# Revit family: Shower-Valve_Trim-KOHLER-Composed-K-T73140BR
name_source: partatom
category: Specialty Equipment
revit_build: Autodesk Revit 2017 (Build: 20160225_1515(x64)
units: mm (PartAtom-declared; Revit-internal decimal feet)

## family parameters
Cut with Voids When Loaded = No
Host = Face
OmniClass Number = 23.31.25.00
OmniClass Title = Toilet and Bath Specialties
Part Type = Normal
Room Calculation Point = No
Round Connector Dimension = Use Diameter
Shared = No

## types (3) — shared parameters
ADA Compliant = Yes
Assembly Code = C1030200
Date Modified = 05/26/2021
Default Elevation = 42"
Description = shower diverter valve
Height = 3 7/8"
Length = 3 5/16"
Manufacturer = KOHLER Co.
Master Format 2014 = 10 28 00
Master Format 2014 Name = Toilet, Bath, and Laundry Accessories
Material = Premium Metal Construction
Product Name = COMPOSED
Product Page URL = https://br.kohler.com
URL = https://br.kohler.com
WaterSense Certified = No
Width = 3 7/8"

## per-type parameters (varying)
| type | Finish | Model | T73140_3 | T73140_4 | Type |
| Lever Handle, TT-Vibrant Titanium | Kohler-Metal-TT-Vibrant_Titanium | K-T73140BR-4-TT | No | Yes | 1 |
| Cross Handle, TT-Vibrant Titanium | Kohler-Metal-TT-Vibrant_Titanium | K-T73140BR-3-TT | Yes | No | 2 |
| Lever Handle, CP-Polished Chrome | Kohler-Metal-CP-Polished_Chrome | K-T73140BR-4-CP | No | Yes | 3 |

## geometry (parser evidence)
native form markers: Sweep x4
no freeform markers — native parametric forms only
